# Revit family: Lighting_Linear_LED_StarTek_Avion1
name_source: partatom
category: Lighting Fixtures
units: mm (PartAtom-declared; Revit-internal decimal feet)

## family parameters
Cut with Voids When Loaded = No
Host = Face
Light Source = Yes
OmniClass Number = 23.80.70.11
OmniClass Title = Luminaries for Internal Lighting
Part Type = Normal
Room Calculation Point = No
Round Connector Dimension = Use Diameter
Shared = No

## types (1)
- Not a Type - Load Type Catalog!
    AC 05 = Mounting : Aircraft Cable with Canopy 5' (AC05)
    AC 10 = Mounting : Aircraft Cable with Canopy 10' (AC10)
    AL05 = Mounting : Aircraft Cable with Loop 5' (AL05)
    AL10 = Mounting : Aircraft Cable with Loop 10' (AL10)
    Apparent Load = 45 VA
    Assembly Code = D5020200
    Color Filter = 16777215
    Default Elevation = 4' - 0"
    Description = Avion
    Dimming Lamp Color Temperature Shift = <None>
    Emit Shape Visible in Rendering = No
    Emit from Rectangle Length = 1' - 5 1/2"
    Emit from Rectangle Width = 0' - 8 1/2"
    Frequency = 60 Hz
    Height = 0' - 2"
    Input Wattage = 45 W
    Keynote = 16500
    Lamp = LED
    Lamp length 18" = Yes
    Lamp length 36" = No
    Length = 1' - 6"
    Manufacturer = StarTek Lighting
    Number of Poles = 1
    Output = Standard
    Phase = 1
    Photometric Note = Import IES files https://starteklightingamerica.com
    Photometric Web File = Generic Light Source Shown : Please download and link the IES file that best matches your fixture specification
    Power Factor = 1
    Product data url = https://www.bimobject.com
    Rigid Pendant (PM) = Mounting : Rigid Pendant (PM) - Specify Length
    Tilt Angle = 90.00°
    Type Comments = Linear Lighting Fixture
    URL = https://starteklightingamerica.com
    Voltage = 120 V
    Voltage Range = 120-277V
    Wattage Comments = Efficacy up to 153 lm/W
    Weight = 6.00 lbf
    Width = 0' - 8 1/2"

## geometry (parser evidence)
native form markers: Sweep x11
no freeform markers — native parametric forms only
